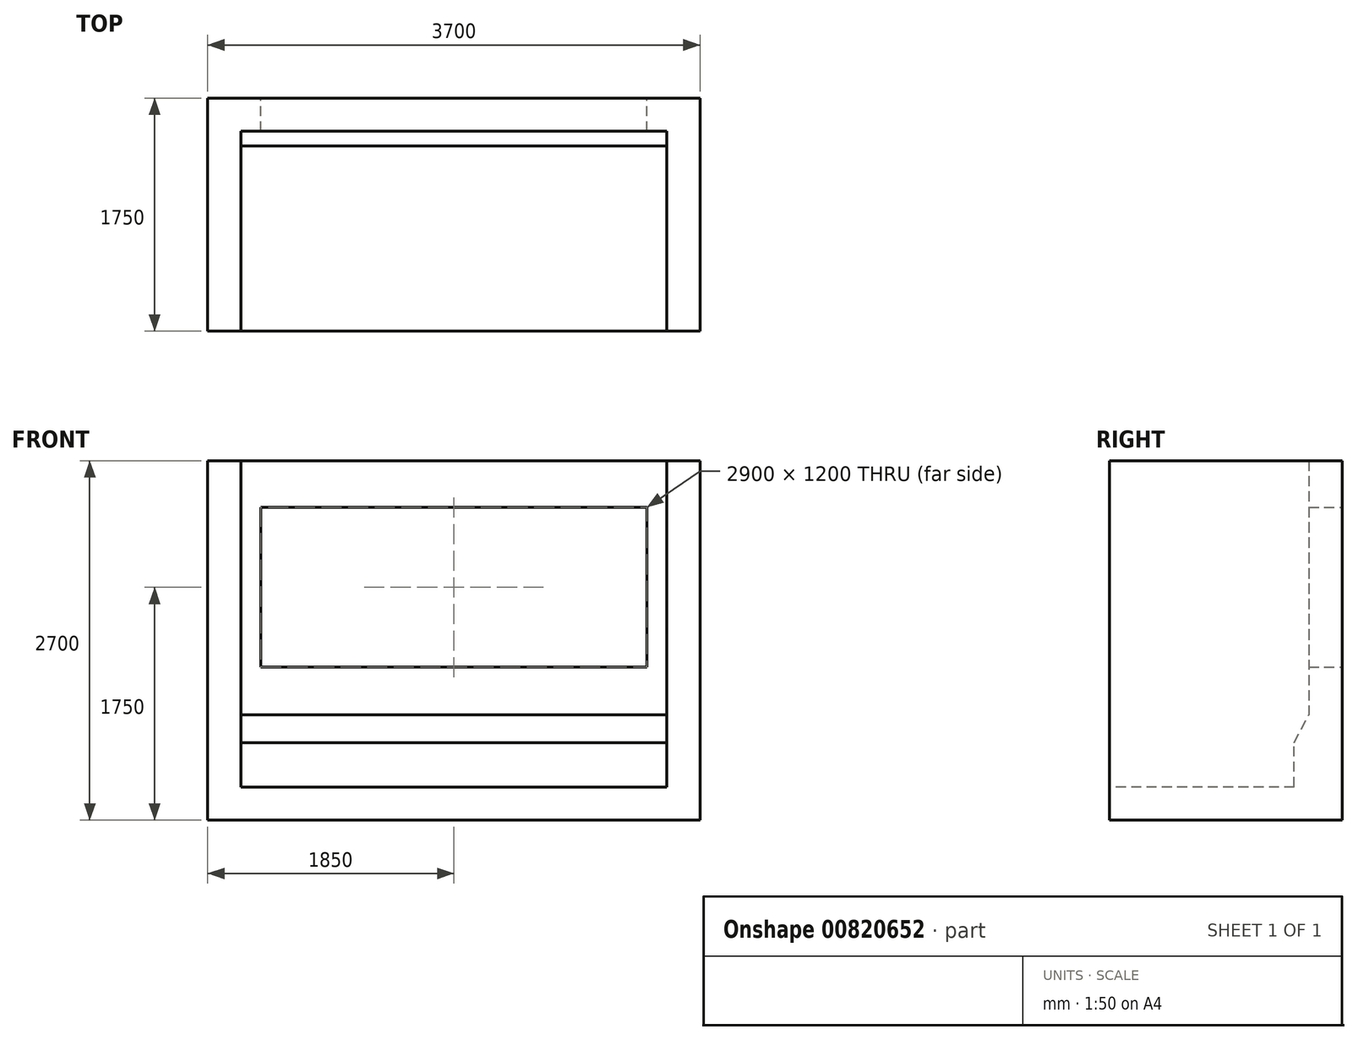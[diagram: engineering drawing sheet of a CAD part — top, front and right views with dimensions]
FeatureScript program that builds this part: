
annotation { "Feature Type Name" : "Feature", "Feature Type Description" : "" }
export const myFeature = defineFeature(function(context is Context, id is Id, definition is map)
    precondition{}
    {
        {
            var Q0;
            Q0=qCreatedBy(makeId("Front.planeOp"),FACE);
            var sketch = newSketch(context, id + "F0", { "sketchPlane" : qUnion([Q0])});
            skLineSegment(sketch, "E0.bottom", {"start": v(1600, 1225) * mm, "end": v(-1600, 1225) * mm});
            skLineSegment(sketch, "E0.top", {"start": v(1600, -1225) * mm, "end": v(-1600, -1225) * mm});
            skLineSegment(sketch, "E0.left", {"start": v(1600, 1225) * mm, "end": v(1600, -1225) * mm});
            skLineSegment(sketch, "E0.right", {"start": v(-1600, 1225) * mm, "end": v(-1600, -1225) * mm});
            skPoint(sketch, "E0.middle", {"position": v(0, 0) * mm});
            skLineSegment(sketch, "E1.bottom", {"start": v(1450, 875) * mm, "end": v(-1450, 875) * mm});
            skLineSegment(sketch, "E1.top", {"start": v(1450, -325) * mm, "end": v(-1450, -325) * mm});
            skLineSegment(sketch, "E1.left", {"start": v(1450, 875) * mm, "end": v(1450, -325) * mm});
            skLineSegment(sketch, "E1.right", {"start": v(-1450, 875) * mm, "end": v(-1450, -325) * mm});
            skPoint(sketch, "E1.middle", {"position": v(0, 275) * mm});
            skSolve(sketch);
        }
        {
            var Q0;
            Q0 = qSketchRegion(id + "F0", true);
            extrude(context, id + "F1", {"entities" : qUnion([Q0]), "depth" : 250 * mm, "offsetDistance" : 25 * mm});
        }
        {
            var Q0;
            Q0=makeQuery(id+"F1.opExtrude","SWEPT_FACE",FACE,{"disambiguationData":[OSD([sQuery(id+"F0.wireOp",EDGE,"E0.left")])]});
            var sketch = newSketch(context, id + "F2", { "sketchPlane" : qUnion([Q0])});
            skLineSegment(sketch, "E2.bottom", {"start": v(0, 1225) * mm, "end": v(-1750, 1225) * mm});
            skLineSegment(sketch, "E2.top", {"start": v(0, -1225) * mm, "end": v(-1750, -1225) * mm});
            skLineSegment(sketch, "E2.left", {"start": v(0, 1225) * mm, "end": v(0, -1225) * mm});
            skLineSegment(sketch, "E2.right", {"start": v(-1750, 1225) * mm, "end": v(-1750, -1225) * mm});
            skSolve(sketch);
        }
        {
            var Q0;
            {var subQ2=sQuery(id+"F2.wireOp",EDGE,"E2.right");Q0=makeQuery(id+"F2.imprint","IMPRINT",FACE,{"disambiguationData":[TD([[makeQuery(id+"F2.imprint","IMPRINT",EDGE,{"derivedFrom":subQ2}),1.0]])]});}
            var Q1;
            {var subQ0=sQuery(id+"F2.wireOp",EDGE,"E2.left");Q1=makeQuery(id+"F2.imprint","IMPRINT",FACE,{"disambiguationData":[TD([[makeQuery(id+"F2.imprint","IMPRINT",EDGE,{"derivedFrom":subQ0}),-1.0]])]});}
            extrude(context, id + "F3", {"entities" : qUnion([Q0, Q1]), "operationType" : NewBodyOperationType.ADD, "depth" : 250 * mm, "offsetDistance" : 25 * mm});
        }
        {
            var Q0;
            Q0=makeQuery(id+"F1.opExtrude","SWEPT_FACE",FACE,{"disambiguationData":[OSD([sQuery(id+"F0.wireOp",EDGE,"E0.right")])]});
            var sketch = newSketch(context, id + "F4", { "sketchPlane" : qUnion([Q0])});
            skLineSegment(sketch, "E3.0", {"start": v(0, 1225) * mm, "end": v(1750, 1225) * mm});
            skLineSegment(sketch, "E4.0", {"start": v(1750, 1225) * mm, "end": v(1750, -1225) * mm});
            skLineSegment(sketch, "E5.0", {"start": v(0, -1225) * mm, "end": v(1750, -1225) * mm});
            skLineSegment(sketch, "E6.0", {"start": v(0, 1225) * mm, "end": v(0, -1225) * mm});
            skSolve(sketch);
        }
        {
            var Q0;
            Q0 = qSketchRegion(id + "F4", true);
            extrude(context, id + "F5", {"entities" : qUnion([Q0]), "operationType" : NewBodyOperationType.ADD, "depth" : 250 * mm, "offsetDistance" : 25 * mm});
        }
        {
            var Q0;
            Q0=makeQuery(id+"F5.boolean.opBoolean","MERGE",FACE,{"derivedFrom":[makeQuery(id+"F3.boolean.opBoolean","MERGE",FACE,{"derivedFrom":[makeQuery(id+"F1.opExtrude","SWEPT_FACE",FACE,{"disambiguationData":[OSD([sQuery(id+"F0.wireOp",EDGE,"E0.top")])]}),makeQuery(id+"F3.opExtrude","SWEPT_FACE",FACE,{"disambiguationData":[OSD([sQuery(id+"F2.wireOp",EDGE,"E2.top")])]})]}),makeQuery(id+"F5.opExtrude","SWEPT_FACE",FACE,{"disambiguationData":[OSD([sQuery(id+"F4.wireOp",EDGE,"E5.0")])]})]});
            var sketch = newSketch(context, id + "F6", { "sketchPlane" : qUnion([Q0])});
            skLineSegment(sketch, "E7.bottom", {"start": v(-1850, 0) * mm, "end": v(1850, 0) * mm});
            skLineSegment(sketch, "E7.top", {"start": v(-1850, 1750) * mm, "end": v(1850, 1750) * mm});
            skLineSegment(sketch, "E7.left", {"start": v(-1850, 0) * mm, "end": v(-1850, 1750) * mm});
            skLineSegment(sketch, "E7.right", {"start": v(1850, 0) * mm, "end": v(1850, 1750) * mm});
            skSolve(sketch);
        }
        {
            var Q0;
            Q0=makeQuery(id+"F6.imprint","IMPRINT",FACE,{"disambiguationData":[TD([[makeQuery(id+"F6.imprint","IMPRINT",EDGE,{"derivedFrom":makeQuery(id+"F1.opExtrude","CAP_EDGE",EDGE,{"disambiguationData":[OSD([sQuery(id+"F0.wireOp",EDGE,"E0.top")])],"isStart":false})}),-1.0]])]});
            var Q1;
            Q1=makeQuery(id+"F6.imprint","IMPRINT",FACE,{"disambiguationData":[TD([[makeQuery(id+"F6.imprint","IMPRINT",EDGE,{"derivedFrom":sQuery(id+"F6.wireOp",EDGE,"E7.bottom")}),-1.0]])]});
            extrude(context, id + "F7", {"entities" : qUnion([Q0, Q1]), "operationType" : NewBodyOperationType.ADD, "depth" : 250 * mm, "offsetDistance" : 25 * mm});
        }
        {
            var Q0;
            Q0=makeQuery(id+"F5.opExtrude","CAP_FACE",FACE,{"disambiguationData":[OSD([sQuery(id+"F4.wireOp",EDGE,"E3.0"),sQuery(id+"F4.wireOp",EDGE,"E4.0"),sQuery(id+"F4.wireOp",EDGE,"E5.0"),sQuery(id+"F4.wireOp",EDGE,"E6.0")])],"isStart":true});
            var sketch = newSketch(context, id + "F8", { "sketchPlane" : qUnion([Q0])});
            skLineSegment(sketch, "E8", {"start": v(-250, -1225) * mm, "end": v(-360, -1225) * mm});
            skLineSegment(sketch, "E9", {"start": v(-360, -1225) * mm, "end": v(-360, -893) * mm});
            skLineSegment(sketch, "E10", {"start": v(-360, -893) * mm, "end": v(-250, -683) * mm});
            skLineSegment(sketch, "E11", {"start": v(-250, -683) * mm, "end": v(-250, -1225) * mm});
            skSolve(sketch);
        }
        {
            var Q0;
            Q0=makeQuery(id+"F8.imprint","IMPRINT",FACE,{"disambiguationData":[TD([[makeQuery(id+"F8.imprint","IMPRINT",EDGE,{"derivedFrom":sQuery(id+"F8.wireOp",EDGE,"E8")}),-1.0]])]});
            extrude(context, id + "F9", {"entities" : qUnion([Q0]), "operationType" : NewBodyOperationType.ADD, "endBound" : BoundingType.UP_TO_NEXT, "depth" : 25 * mm, "offsetDistance" : 25 * mm});
        }
    });
